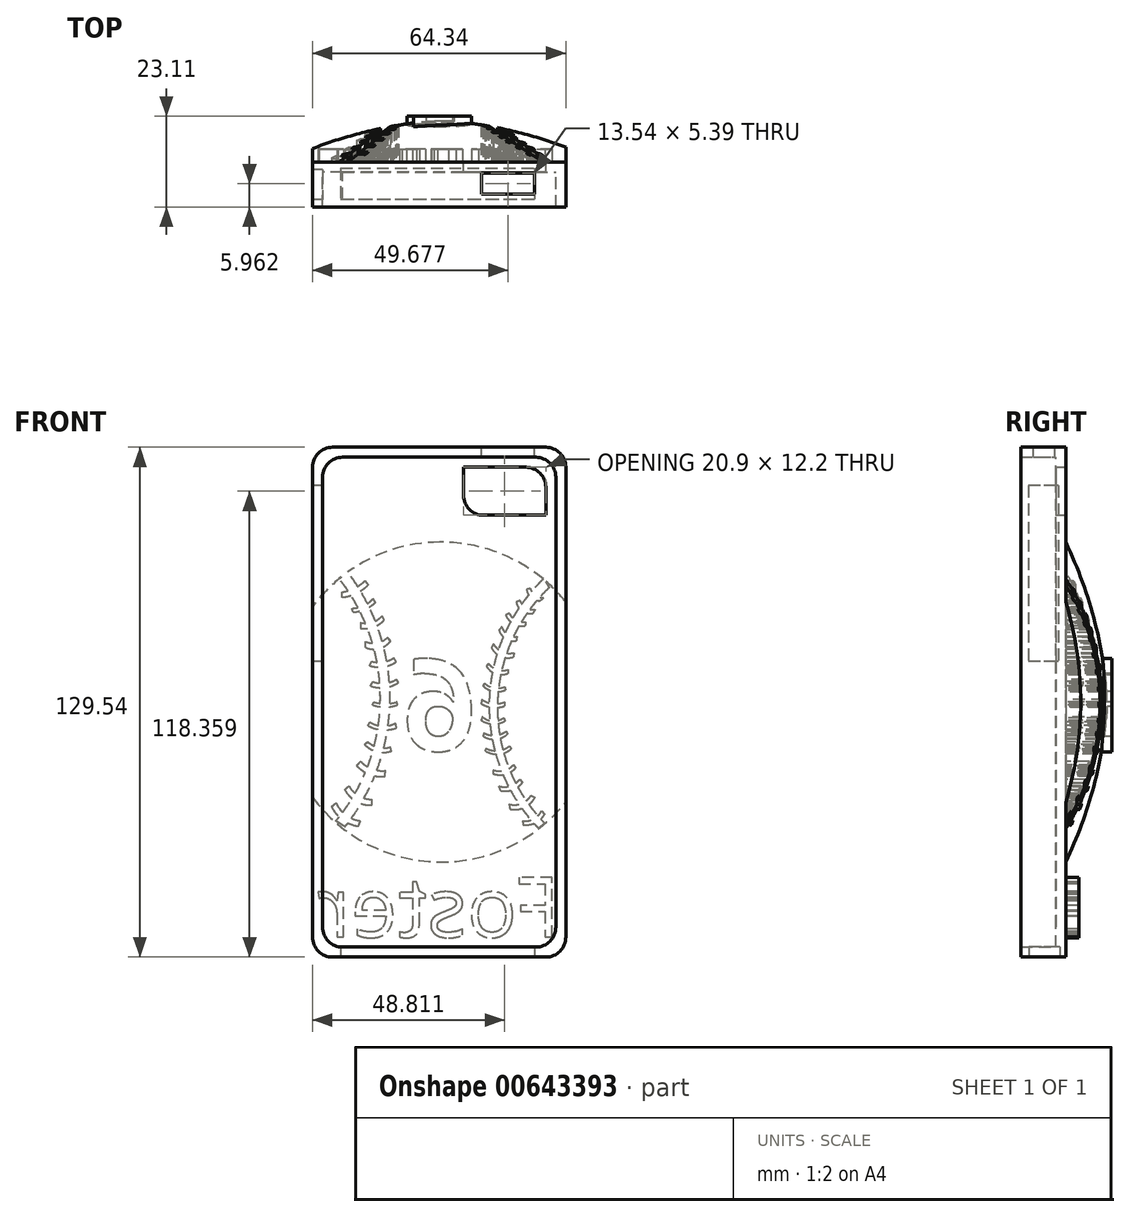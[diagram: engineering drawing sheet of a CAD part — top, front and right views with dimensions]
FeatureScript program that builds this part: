
annotation { "Feature Type Name" : "Feature", "Feature Type Description" : "" }
export const myFeature = defineFeature(function(context is Context, id is Id, definition is map)
    precondition{}
    {
        {
            var Q0;
            Q0=qCreatedBy(makeId("Front.planeOp"),FACE);
            var sketch = newSketch(context, id + "F0", { "sketchPlane" : qUnion([Q0])});
            skLineSegment(sketch, "E0", {"start": v(-32.65, 64.75) * mm, "end": v(-32.65, -64.8) * mm});
            skLineSegment(sketch, "E1", {"start": v(-32.65, -64.8) * mm, "end": v(31.7, -64.8) * mm});
            skLineSegment(sketch, "E2", {"start": v(31.7, -64.8) * mm, "end": v(31.7, 64.75) * mm});
            skLineSegment(sketch, "E3", {"start": v(31.7, 64.75) * mm, "end": v(-32.65, 64.75) * mm});
            skSolve(sketch);
        }
        {
            var Q0;
            Q0=qSketchRegion(id+"F0",true);
            extrude(context, id + "F1", {"entities" : qUnion([Q0]), "depth" : 11.43 * mm, "offsetDistance" : 25.4 * mm});
        }
        {
            var Q0;
            Q0=makeQuery(id+"F1.opExtrude","CAP_FACE",FACE,{"disambiguationData":[OSD([sQuery(id+"F0.wireOp",EDGE,"E0"),sQuery(id+"F0.wireOp",EDGE,"E1"),sQuery(id+"F0.wireOp",EDGE,"E2"),sQuery(id+"F0.wireOp",EDGE,"E3")])],"isStart":false});
            shell(context, id + "F2", {"entities" : qUnion([Q0]), "thickness" : 2.54 * mm});
        }
        {
            var Q0;
            Q0=makeQuery(id+"F2.opShell","OFFSET_EDGE",EDGE,{"disambiguationData":[OSD([sQuery(id+"F0.wireOp",EDGE,"E0"),sQuery(id+"F0.wireOp",EDGE,"E3")])]});
            var Q1;
            Q1=makeQuery(id+"F2.opShell","OFFSET_EDGE",EDGE,{"disambiguationData":[OSD([sQuery(id+"F0.wireOp",EDGE,"E2"),sQuery(id+"F0.wireOp",EDGE,"E3")])]});
            var Q2;
            Q2=makeQuery(id+"F1.opExtrude","SWEPT_EDGE",EDGE,{"disambiguationData":[OSD([sQuery(id+"F0.wireOp",EDGE,"E2"),sQuery(id+"F0.wireOp",EDGE,"E3")])]});
            var Q3;
            Q3=makeQuery(id+"F1.opExtrude","SWEPT_EDGE",EDGE,{"disambiguationData":[OSD([sQuery(id+"F0.wireOp",EDGE,"E0"),sQuery(id+"F0.wireOp",EDGE,"E3")])]});
            fillet(context, id + "F3", {"entities" : qUnion([Q0, Q1, Q2, Q3]), "radius" : 5.08 * mm, "tangentPropagation" : true, "allowEdgeOverflow" : false});
        }
        {
            var Q0;
            Q0=makeQuery(id+"F1.opExtrude","SWEPT_EDGE",EDGE,{"disambiguationData":[OSD([sQuery(id+"F0.wireOp",EDGE,"E0"),sQuery(id+"F0.wireOp",EDGE,"E1")])]});
            var Q1;
            Q1=makeQuery(id+"F1.opExtrude","SWEPT_EDGE",EDGE,{"disambiguationData":[OSD([sQuery(id+"F0.wireOp",EDGE,"E1"),sQuery(id+"F0.wireOp",EDGE,"E2")])]});
            var Q2;
            {var subQ0=sQuery(id+"F0.wireOp",EDGE,"E0");Q2=makeQuery(id+"FT8oDP2O1UVCOSW_1.boolean.opBoolean","SPLIT",EDGE,{"disambiguationData":[topologyDisambiguationEdgeConnected([makeQuery(id+"FT8oDP2O1UVCOSW_1.opExtrude","CAP_FACE",FACE,{"disambiguationData":[OSD([sQuery(id+"FKsIdxiG1m6IwAw_1.wireOp",EDGE,"Qu0jH38F-jogJ-LF4x-abM8-sLSAV8IaNlCL.bottom"),sQuery(id+"FKsIdxiG1m6IwAw_1.wireOp",EDGE,"Qu0jH38F-jogJ-LF4x-abM8-sLSAV8IaNlCL.top"),sQuery(id+"FKsIdxiG1m6IwAw_1.wireOp",EDGE,"Qu0jH38F-jogJ-LF4x-abM8-sLSAV8IaNlCL.left"),sQuery(id+"FKsIdxiG1m6IwAw_1.wireOp",EDGE,"Qu0jH38F-jogJ-LF4x-abM8-sLSAV8IaNlCL.right")])],"isStart":false})])],"derivedFrom":makeQuery(id+"F2.opShell","OFFSET_EDGE",EDGE,{"disambiguationData":[OSD([subQ0,sQuery(id+"F0.wireOp",EDGE,"E1")])]})});}
            var Q3;
            {var subQ0=sQuery(id+"F0.wireOp",EDGE,"E2");Q3=makeQuery(id+"FT8oDP2O1UVCOSW_1.boolean.opBoolean","SPLIT",EDGE,{"disambiguationData":[topologyDisambiguationEdgeConnected([makeQuery(id+"FT8oDP2O1UVCOSW_1.opExtrude","CAP_FACE",FACE,{"disambiguationData":[OSD([sQuery(id+"FKsIdxiG1m6IwAw_1.wireOp",EDGE,"Qu0jH38F-jogJ-LF4x-abM8-sLSAV8IaNlCL.bottom"),sQuery(id+"FKsIdxiG1m6IwAw_1.wireOp",EDGE,"Qu0jH38F-jogJ-LF4x-abM8-sLSAV8IaNlCL.top"),sQuery(id+"FKsIdxiG1m6IwAw_1.wireOp",EDGE,"Qu0jH38F-jogJ-LF4x-abM8-sLSAV8IaNlCL.left"),sQuery(id+"FKsIdxiG1m6IwAw_1.wireOp",EDGE,"Qu0jH38F-jogJ-LF4x-abM8-sLSAV8IaNlCL.right")])],"isStart":false})])],"derivedFrom":makeQuery(id+"F2.opShell","OFFSET_EDGE",EDGE,{"disambiguationData":[OSD([sQuery(id+"F0.wireOp",EDGE,"E1"),subQ0])]})});}
            fillet(context, id + "F4", {"entities" : qUnion([Q0, Q1, Q2, Q3]), "radius" : 5.08 * mm, "tangentPropagation" : true, "allowEdgeOverflow" : false});
        }
        {
            var Q0;
            Q0=makeQuery(id+"F1.opExtrude","SWEPT_FACE",FACE,{"disambiguationData":[OSD([sQuery(id+"F0.wireOp",EDGE,"E1")])]});
            var sketch = newSketch(context, id + "F5", { "sketchPlane" : qUnion([Q0])});
            skLineSegment(sketch, "E4.bottom", {"start": v(-25.48, 1.54) * mm, "end": v(23.7, 1.54) * mm});
            skLineSegment(sketch, "E4.top", {"start": v(-25.48, 9.42) * mm, "end": v(23.7, 9.42) * mm});
            skLineSegment(sketch, "E4.left", {"start": v(-25.48, 1.54) * mm, "end": v(-25.48, 9.42) * mm});
            skLineSegment(sketch, "E4.right", {"start": v(23.7, 1.54) * mm, "end": v(23.7, 9.42) * mm});
            skSolve(sketch);
        }
        {
            var Q0;
            Q0 = qSketchRegion(id + "F5", true);
            extrude(context, id + "F6", {"entities" : qUnion([Q0]), "operationType" : NewBodyOperationType.REMOVE, "oppositeDirection" : true, "depth" : 2.54 * mm, "offsetDistance" : 25.4 * mm});
        }
        {
            var Q0;
            Q0=makeQuery(id+"F1.opExtrude","SWEPT_FACE",FACE,{"disambiguationData":[OSD([sQuery(id+"F0.wireOp",EDGE,"E0")])]});
            var sketch = newSketch(context, id + "F7", { "sketchPlane" : qUnion([Q0])});
            skLineSegment(sketch, "E5.bottom", {"start": v(1.9, 55) * mm, "end": v(9.52, 55) * mm});
            skLineSegment(sketch, "E5.top", {"start": v(1.9, 10.3) * mm, "end": v(9.52, 10.3) * mm});
            skLineSegment(sketch, "E5.left", {"start": v(1.9, 55) * mm, "end": v(1.9, 10.3) * mm});
            skLineSegment(sketch, "E5.right", {"start": v(9.52, 55) * mm, "end": v(9.52, 10.3) * mm});
            skSolve(sketch);
        }
        {
            var Q0;
            Q0 = qSketchRegion(id + "F7", true);
            extrude(context, id + "F8", {"entities" : qUnion([Q0]), "operationType" : NewBodyOperationType.REMOVE, "oppositeDirection" : true, "depth" : 2.54 * mm, "offsetDistance" : 25.4 * mm});
        }
        {
            var Q0;
            Q0=makeQuery(id+"F1.opExtrude","SWEPT_FACE",FACE,{"disambiguationData":[OSD([sQuery(id+"F0.wireOp",EDGE,"E3")])]});
            var sketch = newSketch(context, id + "F9", { "sketchPlane" : qUnion([Q0])});
            skLineSegment(sketch, "E6.bottom", {"start": v(10.26, -8.16) * mm, "end": v(23.8, -8.16) * mm});
            skLineSegment(sketch, "E6.top", {"start": v(10.26, -2.77) * mm, "end": v(23.8, -2.77) * mm});
            skLineSegment(sketch, "E6.left", {"start": v(10.26, -8.16) * mm, "end": v(10.26, -2.77) * mm});
            skLineSegment(sketch, "E6.right", {"start": v(23.8, -8.16) * mm, "end": v(23.8, -2.77) * mm});
            skSolve(sketch);
        }
        {
            var Q0;
            Q0 = qSketchRegion(id + "F9", true);
            extrude(context, id + "F10", {"entities" : qUnion([Q0]), "operationType" : NewBodyOperationType.REMOVE, "oppositeDirection" : true, "depth" : 2.54 * mm, "offsetDistance" : 25.4 * mm});
        }
        {
            var Q0;
            Q0=makeQuery(id+"F1.opExtrude","CAP_FACE",FACE,{"disambiguationData":[OSD([sQuery(id+"F0.wireOp",EDGE,"E0"),sQuery(id+"F0.wireOp",EDGE,"E1"),sQuery(id+"F0.wireOp",EDGE,"E2"),sQuery(id+"F0.wireOp",EDGE,"E3")])],"isStart":true});
            var sketch = newSketch(context, id + "F11", { "sketchPlane" : qUnion([Q0])});
            skLineSegment(sketch, "E7.bottom", {"start": v(-26.61, 59.67) * mm, "end": v(-5.7, 59.67) * mm});
            skLineSegment(sketch, "E7.top", {"start": v(-26.61, 47.47) * mm, "end": v(-5.7, 47.47) * mm});
            skLineSegment(sketch, "E7.left", {"start": v(-26.61, 59.67) * mm, "end": v(-26.61, 47.47) * mm});
            skLineSegment(sketch, "E7.right", {"start": v(-5.7, 59.67) * mm, "end": v(-5.7, 47.47) * mm});
            skSolve(sketch);
        }
        {
            var Q0;
            Q0 = qSketchRegion(id + "F11", true);
            extrude(context, id + "F12", {"entities" : qUnion([Q0]), "operationType" : NewBodyOperationType.REMOVE, "oppositeDirection" : true, "depth" : 2.54 * mm, "offsetDistance" : 25.4 * mm});
        }
        {
            var Q0;
            Q0=makeQuery(id+"F12.boolean.opBoolean","COPY",EDGE,{"derivedFrom":makeQuery(id+"F12.opExtrude","SWEPT_EDGE",EDGE,{"disambiguationData":[OSD([sQuery(id+"F11.wireOp",EDGE,"E7.bottom"),sQuery(id+"F11.wireOp",EDGE,"E7.left")])]})});
            var Q1;
            Q1=makeQuery(id+"F12.boolean.opBoolean","COPY",EDGE,{"derivedFrom":makeQuery(id+"F12.opExtrude","SWEPT_EDGE",EDGE,{"disambiguationData":[OSD([sQuery(id+"F11.wireOp",EDGE,"E7.top"),sQuery(id+"F11.wireOp",EDGE,"E7.right")])]})});
            fillet(context, id + "F13", {"entities" : qUnion([Q0, Q1]), "radius" : 5.08 * mm, "tangentPropagation" : true, "allowEdgeOverflow" : false});
        }
        {
            var Q0;
            Q0=qCreatedBy(makeId("Right.planeOp"),FACE);
            var sketch = newSketch(context, id + "F14", { "sketchPlane" : qUnion([Q0])});
            skLineSegment(sketch, "E8", {"start": v(0, 0) * mm, "end": v(10.6, 0) * mm});
            skLineSegment(sketch, "E9", {"start": v(0, 0) * mm, "end": v(0, 40.64) * mm});
            skArc(sketch, "E10", {"start": v(10.6, 0) * mm, "mid": v(7.26, 20.83) * mm, "end": v(0, 40.64) * mm});
            skSolve(sketch);
        }
        {
            var Q0;
            Q0 = qSketchRegion(id + "F14", true);
            var Q1;
            Q1=sQuery(id+"F14.wireOp",EDGE,"E8");
            revolve(context, id + "F15", {"operationType" : NewBodyOperationType.ADD, "entities" : qUnion([Q0]), "axis" : qUnion([Q1]), "revolveType" : RevolveType.FULL});
        }
        {
            var Q0;
            {var subQ0=sQuery(id+"F0.wireOp",EDGE,"E2");Q0=makeQuery(id+"F15.boolean.opBoolean","SPLIT",FACE,{"disambiguationData":[TD([makeQuery(id+"F1.opExtrude","SWEPT_FACE",FACE,{"disambiguationData":[OSD([subQ0])]})])],"derivedFrom":makeQuery(id+"F15.opRevolve","SWEPT_FACE",FACE,{"disambiguationData":[OSD([sQuery(id+"F14.wireOp",EDGE,"E9")])]})});}
            var sketch = newSketch(context, id + "F16", { "sketchPlane" : qUnion([Q0])});
            skLineSegment(sketch, "E11", {"start": v(31.7, 25.44) * mm, "end": v(31.7, -25.44) * mm});
            skLineSegment(sketch, "E12", {"start": v(31.7, -25.44) * mm, "end": v(46.9, -25.44) * mm});
            skLineSegment(sketch, "E13", {"start": v(46.9, -25.44) * mm, "end": v(46.9, 25.44) * mm});
            skLineSegment(sketch, "E14", {"start": v(46.9, 25.44) * mm, "end": v(31.7, 25.44) * mm});
            skSolve(sketch);
        }
        {
            var Q0;
            Q0 = qSketchRegion(id + "F16", true);
            extrude(context, id + "F17", {"entities" : qUnion([Q0]), "operationType" : NewBodyOperationType.REMOVE, "oppositeDirection" : true, "depth" : 13.97 * mm, "offsetDistance" : 25.4 * mm});
        }
        {
            var Q0;
            {var subQ0=sQuery(id+"F0.wireOp",EDGE,"E0");Q0=makeQuery(id+"F15.boolean.opBoolean","SPLIT",FACE,{"disambiguationData":[TD([makeQuery(id+"F1.opExtrude","SWEPT_FACE",FACE,{"disambiguationData":[OSD([subQ0])]})])],"derivedFrom":makeQuery(id+"F15.opRevolve","SWEPT_FACE",FACE,{"disambiguationData":[OSD([sQuery(id+"F14.wireOp",EDGE,"E9")])]})});}
            var sketch = newSketch(context, id + "F18", { "sketchPlane" : qUnion([Q0])});
            skLineSegment(sketch, "E15", {"start": v(-32.65, 24.2) * mm, "end": v(-32.65, -24.2) * mm});
            skLineSegment(sketch, "E16", {"start": v(-32.65, -24.2) * mm, "end": v(-43.03, -24.2) * mm});
            skLineSegment(sketch, "E17", {"start": v(-43.03, -24.2) * mm, "end": v(-43.03, 24.2) * mm});
            skLineSegment(sketch, "E18", {"start": v(-43.03, 24.2) * mm, "end": v(-32.65, 24.2) * mm});
            skSolve(sketch);
        }
        {
            var Q0;
            Q0 = qSketchRegion(id + "F18", true);
            extrude(context, id + "F19", {"entities" : qUnion([Q0]), "operationType" : NewBodyOperationType.REMOVE, "oppositeDirection" : true, "depth" : 11.43 * mm, "offsetDistance" : 25.4 * mm});
        }
        {
            var Q0;
            Q0=qCreatedBy(makeId("Front.planeOp"),FACE);
            var sketch = newSketch(context, id + "F20", { "sketchPlane" : qUnion([Q0])});
            skArc(sketch, "E19", {"start": v(-24.38, -31.68) * mm, "mid": v(-12.98, 0.63) * mm, "end": v(-23.8, 33.14) * mm});
            skArc(sketch, "E20", {"start": v(-26.72, -30.22) * mm, "mid": v(-15.42, 0.4) * mm, "end": v(-25.86, 31.31) * mm});
            skLineSegment(sketch, "E21", {"start": v(-23.8, 33.14) * mm, "end": v(-25.86, 31.31) * mm});
            skLineSegment(sketch, "E22", {"start": v(-24.38, -31.68) * mm, "end": v(-26.72, -30.22) * mm});
            skLineSegment(sketch, "E23", {"start": v(-25.86, 31.31) * mm, "end": v(-23.8, 33.14) * mm});
            skSolve(sketch);
        }
        {
            var Q0;
            Q0=qCreatedBy(makeId("Front.planeOp"),FACE);
            var sketch = newSketch(context, id + "F21", { "sketchPlane" : qUnion([Q0])});
            skLineSegment(sketch, "E24", {"start": v(32.56, -30.8) * mm, "end": v(26.43, -30.8) * mm});
            skArc(sketch, "E25", {"start": v(27.55, 29.14) * mm, "mid": v(14.35, -0.61) * mm, "end": v(26.4, -30.85) * mm});
            skArc(sketch, "E26", {"start": v(26.22, 31.47) * mm, "mid": v(12.23, 0) * mm, "end": v(24.78, -32.1) * mm});
            skLineSegment(sketch, "E27", {"start": v(26.43, -30.8) * mm, "end": v(24.78, -32.1) * mm});
            skLineSegment(sketch, "E28", {"start": v(27.55, 29.14) * mm, "end": v(26.22, 31.47) * mm});
            skSolve(sketch);
        }
        {
            var Q0;
            Q0=makeQuery(id+"F20.imprint","IMPRINT",FACE,{"disambiguationData":[TD([[makeQuery(id+"F20.imprint","IMPRINT",EDGE,{"derivedFrom":sQuery(id+"F20.wireOp",EDGE,"E19")}),1.0]])]});
            extrude(context, id + "F22", {"entities" : qUnion([Q0]), "operationType" : NewBodyOperationType.REMOVE, "oppositeDirection" : true, "depth" : 25.4 * mm, "offsetDistance" : 25.4 * mm});
        }
        {
            var Q0;
            {var subQ4=sQuery(id+"F21.wireOp",EDGE,"E26");Q0=makeQuery(id+"F21.imprint","IMPRINT",FACE,{"disambiguationData":[TD([[makeQuery(id+"F21.imprint","IMPRINT",EDGE,{"derivedFrom":subQ4}),1.0]])]});}
            extrude(context, id + "F23", {"entities" : qUnion([Q0]), "operationType" : NewBodyOperationType.REMOVE, "oppositeDirection" : true, "depth" : 13.72 * mm, "offsetDistance" : 25.4 * mm});
        }
        {
            var Q0;
            Q0=qCreatedBy(makeId("Front.planeOp"),FACE);
            var sketch = newSketch(context, id + "F24", { "sketchPlane" : qUnion([Q0])});
            skArc(sketch, "E29", {"start": v(13.33, 14.78) * mm, "mid": v(15.54, 12.78) * mm, "end": v(18.5, 12.52) * mm});
            skArc(sketch, "E30", {"start": v(12.8, 13.85) * mm, "mid": v(15.18, 11.6) * mm, "end": v(18.44, 11.46) * mm});
            skPoint(sketch, "E30.midSnap0", {"position": v(15.54, 12.78) * mm});
            skArc(sketch, "E31", {"start": v(12.05, 9.81) * mm, "mid": v(14.3, 8.24) * mm, "end": v(17.03, 8.25) * mm});
            skArc(sketch, "E32", {"start": v(11.51, 9.17) * mm, "mid": v(13.91, 7.17) * mm, "end": v(17.03, 7.33) * mm});
            skArc(sketch, "E33", {"start": v(11.1, 4.73) * mm, "mid": v(13.54, 3.58) * mm, "end": v(16.22, 3.9) * mm});
            skArc(sketch, "E34", {"start": v(10.61, 4.18) * mm, "mid": v(13.31, 2.72) * mm, "end": v(16.36, 3.07) * mm});
            skArc(sketch, "E35", {"start": v(10.38, 0.62) * mm, "mid": v(13.18, -0.4) * mm, "end": v(16.14, 0) * mm});
            skArc(sketch, "E36", {"start": v(10.16, -0.4) * mm, "mid": v(13.06, -1.38) * mm, "end": v(16.1, -1.01) * mm});
            skLineSegment(sketch, "E37", {"start": v(17.03, 8.25) * mm, "end": v(17.03, 7.33) * mm});
            skLineSegment(sketch, "E38", {"start": v(12.05, 9.81) * mm, "end": v(11.51, 9.17) * mm});
            skLineSegment(sketch, "E39", {"start": v(16.22, 3.9) * mm, "end": v(16.36, 3.07) * mm});
            skLineSegment(sketch, "E40", {"start": v(11.1, 4.73) * mm, "end": v(10.61, 4.18) * mm});
            skLineSegment(sketch, "E41", {"start": v(10.38, 0.62) * mm, "end": v(10.16, -0.4) * mm});
            skLineSegment(sketch, "E42", {"start": v(16.14, 0) * mm, "end": v(16.1, -1.01) * mm});
            skLineSegment(sketch, "E43", {"start": v(18.5, 12.52) * mm, "end": v(18.44, 11.46) * mm});
            skLineSegment(sketch, "E44", {"start": v(13.33, 14.78) * mm, "end": v(12.8, 13.85) * mm});
            skArc(sketch, "E45", {"start": v(10.48, -3.76) * mm, "mid": v(13.2, -4.8) * mm, "end": v(15.97, -4) * mm});
            skArc(sketch, "E46", {"start": v(10.2, -4.62) * mm, "mid": v(13.17, -5.57) * mm, "end": v(16.2, -4.85) * mm});
            skArc(sketch, "E47", {"start": v(10.92, -7.86) * mm, "mid": v(13.8, -8.47) * mm, "end": v(16.55, -7.4) * mm});
            skArc(sketch, "E48", {"start": v(10.69, -8.65) * mm, "mid": v(13.88, -9.46) * mm, "end": v(16.89, -8.14) * mm});
            skArc(sketch, "E49", {"start": v(11.41, -11.78) * mm, "mid": v(14.5, -12.35) * mm, "end": v(17.41, -11.16) * mm});
            skArc(sketch, "E50", {"start": v(11.17, -12.35) * mm, "mid": v(14.58, -13.24) * mm, "end": v(17.84, -11.9) * mm});
            skPoint(sketch, "E50.startSnap0", {"position": v(14.5, -12.35) * mm});
            skArc(sketch, "E51", {"start": v(17.27, -25.92) * mm, "mid": v(20.45, -25.78) * mm, "end": v(22.88, -23.72) * mm});
            skArc(sketch, "E52", {"start": v(17.5, -27.2) * mm, "mid": v(21.17, -26.78) * mm, "end": v(23.85, -24.27) * mm});
            skArc(sketch, "E53", {"start": v(20.73, -30.15) * mm, "mid": v(23.54, -29.72) * mm, "end": v(25.5, -27.67) * mm});
            skArc(sketch, "E54", {"start": v(20.82, -31.16) * mm, "mid": v(24, -30.69) * mm, "end": v(26.33, -28.5) * mm});
            skLineSegment(sketch, "E55", {"start": v(22.88, -23.72) * mm, "end": v(23.85, -24.27) * mm});
            skLineSegment(sketch, "E56", {"start": v(17.27, -25.92) * mm, "end": v(17.5, -27.2) * mm});
            skLineSegment(sketch, "E57", {"start": v(15.97, -4) * mm, "end": v(16.2, -4.85) * mm});
            skLineSegment(sketch, "E58", {"start": v(10.48, -3.76) * mm, "end": v(10.2, -4.62) * mm});
            skLineSegment(sketch, "E59", {"start": v(16.55, -7.4) * mm, "end": v(16.89, -8.14) * mm});
            skLineSegment(sketch, "E60", {"start": v(10.92, -7.86) * mm, "end": v(10.69, -8.65) * mm});
            skLineSegment(sketch, "E61", {"start": v(11.41, -11.78) * mm, "end": v(11.17, -12.35) * mm});
            skLineSegment(sketch, "E62", {"start": v(17.41, -11.16) * mm, "end": v(17.84, -11.9) * mm});
            skLineSegment(sketch, "E63", {"start": v(20.73, -30.15) * mm, "end": v(20.82, -31.16) * mm});
            skLineSegment(sketch, "E64", {"start": v(25.5, -27.67) * mm, "end": v(26.33, -28.5) * mm});
            skArc(sketch, "E65", {"start": v(13.3, -17.27) * mm, "mid": v(16.06, -17.4) * mm, "end": v(18.4, -15.92) * mm});
            skArc(sketch, "E66", {"start": v(13.15, -18.19) * mm, "mid": v(16.27, -18.34) * mm, "end": v(18.96, -16.77) * mm});
            skArc(sketch, "E67", {"start": v(14.78, -21.37) * mm, "mid": v(17.67, -21.3) * mm, "end": v(20.02, -19.6) * mm});
            skArc(sketch, "E68", {"start": v(15.14, -22.5) * mm, "mid": v(18.18, -22.3) * mm, "end": v(20.66, -20.52) * mm});
            skLineSegment(sketch, "E69", {"start": v(13.3, -17.27) * mm, "end": v(13.15, -18.19) * mm});
            skLineSegment(sketch, "E70", {"start": v(18.4, -15.92) * mm, "end": v(18.96, -16.77) * mm});
            skLineSegment(sketch, "E71", {"start": v(20.02, -19.6) * mm, "end": v(20.66, -20.52) * mm});
            skLineSegment(sketch, "E72", {"start": v(15.14, -22.5) * mm, "end": v(14.78, -21.37) * mm});
            skArc(sketch, "E73", {"start": v(14.7, 18.26) * mm, "mid": v(16.42, 16.12) * mm, "end": v(19.1, 15.52) * mm});
            skArc(sketch, "E74", {"start": v(15.44, 19.09) * mm, "mid": v(16.92, 17.17) * mm, "end": v(19.28, 16.62) * mm});
            skArc(sketch, "E75", {"start": v(16.42, 22.1) * mm, "mid": v(18.44, 19.9) * mm, "end": v(21.39, 19.36) * mm});
            skPoint(sketch, "E75.startSnap0", {"position": v(16.42, 16.12) * mm});
            skArc(sketch, "E76", {"start": v(17.36, 22.56) * mm, "mid": v(19.03, 20.73) * mm, "end": v(21.48, 20.37) * mm});
            skArc(sketch, "E77", {"start": v(19.1, 25.4) * mm, "mid": v(20.63, 23.14) * mm, "end": v(23.3, 22.56) * mm});
            skArc(sketch, "E78", {"start": v(20.02, 25.77) * mm, "mid": v(21.57, 24) * mm, "end": v(23.86, 23.48) * mm});
            skArc(sketch, "E79", {"start": v(21.75, 28.6) * mm, "mid": v(22.94, 26.44) * mm, "end": v(25.32, 25.77) * mm});
            skArc(sketch, "E80", {"start": v(22.67, 28.88) * mm, "mid": v(23.94, 27.1) * mm, "end": v(26.05, 26.59) * mm});
            skLineSegment(sketch, "E81", {"start": v(19.28, 16.62) * mm, "end": v(19.1, 15.52) * mm});
            skLineSegment(sketch, "E82", {"start": v(15.44, 19.09) * mm, "end": v(14.7, 18.26) * mm});
            skLineSegment(sketch, "E83", {"start": v(17.36, 22.56) * mm, "end": v(16.42, 22.1) * mm});
            skLineSegment(sketch, "E84", {"start": v(21.48, 20.37) * mm, "end": v(21.39, 19.36) * mm});
            skLineSegment(sketch, "E85", {"start": v(23.86, 23.48) * mm, "end": v(23.3, 22.56) * mm});
            skLineSegment(sketch, "E86", {"start": v(20.02, 25.77) * mm, "end": v(19.1, 25.4) * mm});
            skLineSegment(sketch, "E87", {"start": v(26.05, 26.59) * mm, "end": v(25.32, 25.77) * mm});
            skLineSegment(sketch, "E88", {"start": v(22.67, 28.88) * mm, "end": v(21.75, 28.6) * mm});
            skLineSegment(sketch, "E89.MirrorCS", {"start": v(-12.05, 9.81) * mm, "end": v(-11.51, 9.17) * mm});
            skSolve(sketch);
        }
        {
            var Q0;
            Q0 = qSketchRegion(id + "F24", true);
            extrude(context, id + "F25", {"entities" : qUnion([Q0]), "operationType" : NewBodyOperationType.REMOVE, "oppositeDirection" : true, "depth" : 25.4 * mm, "offsetDistance" : 25.4 * mm});
        }
        {
            var Q0;
            Q0=qCreatedBy(makeId("Front.planeOp"),FACE);
            var sketch = newSketch(context, id + "F26", { "sketchPlane" : qUnion([Q0])});
            skArc(sketch, "E90", {"start": v(-25.18, 27.94) * mm, "mid": v(-22, 28.92) * mm, "end": v(-19.29, 30.82) * mm});
            skArc(sketch, "E91", {"start": v(-25.18, 26.63) * mm, "mid": v(-21.56, 27.6) * mm, "end": v(-18.5, 29.77) * mm});
            skLineSegment(sketch, "E92", {"start": v(-25.18, 26.63) * mm, "end": v(-25.18, 27.94) * mm});
            skLineSegment(sketch, "E93", {"start": v(-19.29, 30.82) * mm, "end": v(-18.5, 29.77) * mm});
            skArc(sketch, "E94", {"start": v(-22.64, 23.82) * mm, "mid": v(-19.67, 24.49) * mm, "end": v(-17.23, 26.29) * mm});
            skArc(sketch, "E95", {"start": v(-22.34, 22.83) * mm, "mid": v(-19.3, 23.61) * mm, "end": v(-16.64, 25.3) * mm});
            skLineSegment(sketch, "E96", {"start": v(-16.64, 25.3) * mm, "end": v(-17.23, 26.29) * mm});
            skLineSegment(sketch, "E97", {"start": v(-22.34, 22.83) * mm, "end": v(-22.64, 23.82) * mm});
            skArc(sketch, "E98", {"start": v(-20.41, 20.2) * mm, "mid": v(-17.45, 20.26) * mm, "end": v(-14.98, 21.9) * mm});
            skArc(sketch, "E99", {"start": v(-20.41, 18.73) * mm, "mid": v(-17.14, 19.04) * mm, "end": v(-14.41, 20.88) * mm});
            skLineSegment(sketch, "E100", {"start": v(-14.41, 20.88) * mm, "end": v(-14.98, 21.9) * mm});
            skLineSegment(sketch, "E101", {"start": v(-20.41, 20.2) * mm, "end": v(-20.41, 18.73) * mm});
            skPoint(sketch, "E102.endSnap0", {"position": v(-15.84, 15.35) * mm});
            skPoint(sketch, "E103.endSnap0", {"position": v(-14.7, 8.8) * mm});
            skArc(sketch, "E104", {"start": v(-17.26, 5.19) * mm, "mid": v(-14.22, 4.77) * mm, "end": v(-11.32, 5.78) * mm});
            skArc(sketch, "E105", {"start": v(-17.94, 4.12) * mm, "mid": v(-14.28, 3.68) * mm, "end": v(-10.82, 4.95) * mm});
            skLineSegment(sketch, "E106", {"start": v(-10.82, 4.95) * mm, "end": v(-11.32, 5.78) * mm});
            skLineSegment(sketch, "E107", {"start": v(-17.94, 4.12) * mm, "end": v(-17.26, 5.19) * mm});
            skArc(sketch, "E108", {"start": v(-20.43, -15.07) * mm, "mid": v(-17.54, -16.99) * mm, "end": v(-14.11, -17.42) * mm});
            skArc(sketch, "E109", {"start": v(-21.4, -16.16) * mm, "mid": v(-18.14, -18.4) * mm, "end": v(-14.22, -18.88) * mm});
            skLineSegment(sketch, "E110", {"start": v(-14.22, -18.88) * mm, "end": v(-14.11, -17.42) * mm});
            skLineSegment(sketch, "E111", {"start": v(-21.4, -16.16) * mm, "end": v(-20.43, -15.07) * mm});
            skPoint(sketch, "E112.endSnap0", {"position": v(-15.94, -12.85) * mm});
            skArc(sketch, "E113", {"start": v(-26.63, -25.65) * mm, "mid": v(-24.15, -28.73) * mm, "end": v(-20.47, -30.16) * mm});
            skArc(sketch, "E114", {"start": v(-27.83, -26.5) * mm, "mid": v(-25.06, -29.89) * mm, "end": v(-21, -31.53) * mm});
            skLineSegment(sketch, "E115", {"start": v(-21, -31.53) * mm, "end": v(-20.47, -30.16) * mm});
            skLineSegment(sketch, "E116", {"start": v(-27.83, -26.5) * mm, "end": v(-26.63, -25.65) * mm});
            skArc(sketch, "E117", {"start": v(-23.38, -21.29) * mm, "mid": v(-20.93, -23.82) * mm, "end": v(-17.52, -24.71) * mm});
            skArc(sketch, "E118", {"start": v(-24.42, -22.32) * mm, "mid": v(-21.53, -25.26) * mm, "end": v(-17.52, -26.18) * mm});
            skLineSegment(sketch, "E119", {"start": v(-17.52, -26.18) * mm, "end": v(-17.52, -24.71) * mm});
            skLineSegment(sketch, "E120", {"start": v(-24.42, -22.32) * mm, "end": v(-23.38, -21.29) * mm});
            skArc(sketch, "E121", {"start": v(-19.14, 15.35) * mm, "mid": v(-16.22, 15.04) * mm, "end": v(-13.61, 16.39) * mm});
            skArc(sketch, "E122", {"start": v(-19.14, 13.88) * mm, "mid": v(-15.66, 13.58) * mm, "end": v(-12.79, 15.56) * mm});
            skLineSegment(sketch, "E123", {"start": v(-12.79, 15.56) * mm, "end": v(-13.61, 16.39) * mm});
            skLineSegment(sketch, "E124", {"start": v(-19.14, 13.88) * mm, "end": v(-19.14, 15.35) * mm});
            skArc(sketch, "E125", {"start": v(-17.04, 0) * mm, "mid": v(-14.14, -0.42) * mm, "end": v(-11.24, 0) * mm});
            skArc(sketch, "E126", {"start": v(-17.36, -0.72) * mm, "mid": v(-14.19, -1.27) * mm, "end": v(-11, -0.72) * mm});
            skLineSegment(sketch, "E127", {"start": v(-11, -0.72) * mm, "end": v(-11.24, 0) * mm});
            skLineSegment(sketch, "E128", {"start": v(-17.36, -0.72) * mm, "end": v(-17.04, 0) * mm});
            skArc(sketch, "E129", {"start": v(-17.62, 10.3) * mm, "mid": v(-14.7, 10.18) * mm, "end": v(-11.95, 11.22) * mm});
            skArc(sketch, "E130", {"start": v(-18.1, 9.25) * mm, "mid": v(-14.62, 8.95) * mm, "end": v(-11.37, 10.21) * mm});
            skLineSegment(sketch, "E131", {"start": v(-11.37, 10.21) * mm, "end": v(-11.95, 11.22) * mm});
            skLineSegment(sketch, "E132", {"start": v(-18.1, 9.25) * mm, "end": v(-17.62, 10.3) * mm});
            skArc(sketch, "E133", {"start": v(-18, -5.11) * mm, "mid": v(-14.8, -6.1) * mm, "end": v(-11.55, -5.35) * mm});
            skArc(sketch, "E134", {"start": v(-18.59, -5.99) * mm, "mid": v(-15, -7.06) * mm, "end": v(-11.3, -6.55) * mm});
            skLineSegment(sketch, "E135", {"start": v(-11.3, -6.55) * mm, "end": v(-11.55, -5.35) * mm});
            skLineSegment(sketch, "E136", {"start": v(-18.59, -5.99) * mm, "end": v(-18, -5.11) * mm});
            skArc(sketch, "E137", {"start": v(-18.65, -10.08) * mm, "mid": v(-15.92, -11.5) * mm, "end": v(-12.84, -11.44) * mm});
            skArc(sketch, "E138", {"start": v(-19.45, -10.77) * mm, "mid": v(-16.27, -12.6) * mm, "end": v(-12.61, -12.47) * mm});
            skLineSegment(sketch, "E139", {"start": v(-12.61, -12.47) * mm, "end": v(-12.84, -11.44) * mm});
            skLineSegment(sketch, "E140", {"start": v(-19.45, -10.77) * mm, "end": v(-18.65, -10.08) * mm});
            skSolve(sketch);
        }
        {
            var Q0;
            Q0 = qSketchRegion(id + "F26", true);
            extrude(context, id + "F27", {"entities" : qUnion([Q0]), "operationType" : NewBodyOperationType.REMOVE, "oppositeDirection" : true, "depth" : 11.18 * mm, "offsetDistance" : 25.4 * mm});
        }
        {
            var Q0;
            {var subQ0=sQuery(id+"F0.wireOp",EDGE,"E2");var subQ1=sQuery(id+"F0.wireOp",EDGE,"E1");var subQ2=sQuery(id+"F0.wireOp",EDGE,"E0");Q0=makeQuery(id+"F15.boolean.opBoolean","SPLIT",FACE,{"disambiguationData":[TD([makeQuery(id+"F1.opExtrude","SWEPT_FACE",FACE,{"disambiguationData":[OSD([subQ1])]})])],"derivedFrom":makeQuery(id+"F1.opExtrude","CAP_FACE",FACE,{"disambiguationData":[OSD([subQ2,subQ1,subQ0,sQuery(id+"F0.wireOp",EDGE,"E3")])],"isStart":true})});}
            var sketch = newSketch(context, id + "F28", { "sketchPlane" : qUnion([Q0])});
            skText(sketch, "E141", { "text": "Foster", "fontName": "OpenSans-Regular.ttf"});
            const initialGuessF28  = {"E141": [-0.03029, -0.05971, 1, 0, 0.01526]};
            skSetInitialGuess(sketch, initialGuessF28);
            skSolve(sketch);
        }
        {
            var Q0;
            Q0 = qSketchRegion(id + "F28", true);
            extrude(context, id + "F29", {"entities" : qUnion([Q0]), "operationType" : NewBodyOperationType.ADD, "depth" : 3.3 * mm, "offsetDistance" : 25.4 * mm});
        }
        {
            var Q0;
            {var subQ2=sQuery(id+"F0.wireOp",EDGE,"E3");var subQ3=sQuery(id+"F0.wireOp",EDGE,"E2");var subQ6=sQuery(id+"F0.wireOp",EDGE,"E0");Q0=makeQuery(id+"F27.boolean.opBoolean","MERGE",FACE,{"derivedFrom":[makeQuery(id+"F25.boolean.opBoolean","MERGE",FACE,{"derivedFrom":[makeQuery(id+"F23.boolean.opBoolean","MERGE",FACE,{"derivedFrom":[makeQuery(id+"F22.boolean.opBoolean","MERGE",FACE,{"derivedFrom":[makeQuery(id+"F15.boolean.opBoolean","SPLIT",FACE,{"disambiguationData":[TD([makeQuery(id+"F1.opExtrude","SWEPT_FACE",FACE,{"disambiguationData":[OSD([subQ2])]})])],"derivedFrom":makeQuery(id+"F1.opExtrude","CAP_FACE",FACE,{"disambiguationData":[OSD([subQ6,sQuery(id+"F0.wireOp",EDGE,"E1"),subQ3,subQ2])],"isStart":true})}),makeQuery(id+"F22.opExtrude","CAP_FACE",FACE,{"disambiguationData":[OSD([sQuery(id+"F20.wireOp",EDGE,"E19"),sQuery(id+"F20.wireOp",EDGE,"E20"),sQuery(id+"F20.wireOp",EDGE,"E22"),sQuery(id+"F20.wireOp",EDGE,"E23")])],"isStart":true})]}),makeQuery(id+"F23.opExtrude","CAP_FACE",FACE,{"disambiguationData":[OSD([sQuery(id+"F21.wireOp",EDGE,"E25"),sQuery(id+"F21.wireOp",EDGE,"E26"),sQuery(id+"F21.wireOp",EDGE,"E27"),sQuery(id+"F21.wireOp",EDGE,"E28")])],"isStart":true})]}),makeQuery(id+"F25.opExtrude","CAP_FACE",FACE,{"disambiguationData":[OSD([sQuery(id+"F24.wireOp",EDGE,"E29"),sQuery(id+"F24.wireOp",EDGE,"E30"),sQuery(id+"F24.wireOp",EDGE,"E43"),sQuery(id+"F24.wireOp",EDGE,"E44")])],"isStart":true}),makeQuery(id+"F25.opExtrude","CAP_FACE",FACE,{"disambiguationData":[OSD([sQuery(id+"F24.wireOp",EDGE,"E31"),sQuery(id+"F24.wireOp",EDGE,"E32"),sQuery(id+"F24.wireOp",EDGE,"E37"),sQuery(id+"F24.wireOp",EDGE,"E38")])],"isStart":true}),makeQuery(id+"F25.opExtrude","CAP_FACE",FACE,{"disambiguationData":[OSD([sQuery(id+"F24.wireOp",EDGE,"E33"),sQuery(id+"F24.wireOp",EDGE,"E34"),sQuery(id+"F24.wireOp",EDGE,"E39"),sQuery(id+"F24.wireOp",EDGE,"E40")])],"isStart":true}),makeQuery(id+"F25.opExtrude","CAP_FACE",FACE,{"disambiguationData":[OSD([sQuery(id+"F24.wireOp",EDGE,"E35"),sQuery(id+"F24.wireOp",EDGE,"E36"),sQuery(id+"F24.wireOp",EDGE,"E41"),sQuery(id+"F24.wireOp",EDGE,"E42")])],"isStart":true}),makeQuery(id+"F25.opExtrude","CAP_FACE",FACE,{"disambiguationData":[OSD([sQuery(id+"F24.wireOp",EDGE,"E45"),sQuery(id+"F24.wireOp",EDGE,"E46"),sQuery(id+"F24.wireOp",EDGE,"E57"),sQuery(id+"F24.wireOp",EDGE,"E58")])],"isStart":true}),makeQuery(id+"F25.opExtrude","CAP_FACE",FACE,{"disambiguationData":[OSD([sQuery(id+"F24.wireOp",EDGE,"E47"),sQuery(id+"F24.wireOp",EDGE,"E48"),sQuery(id+"F24.wireOp",EDGE,"E59"),sQuery(id+"F24.wireOp",EDGE,"E60")])],"isStart":true}),makeQuery(id+"F25.opExtrude","CAP_FACE",FACE,{"disambiguationData":[OSD([sQuery(id+"F24.wireOp",EDGE,"E49"),sQuery(id+"F24.wireOp",EDGE,"E50"),sQuery(id+"F24.wireOp",EDGE,"E61"),sQuery(id+"F24.wireOp",EDGE,"E62")])],"isStart":true}),makeQuery(id+"F25.opExtrude","CAP_FACE",FACE,{"disambiguationData":[OSD([sQuery(id+"F24.wireOp",EDGE,"E51"),sQuery(id+"F24.wireOp",EDGE,"E52"),sQuery(id+"F24.wireOp",EDGE,"E55"),sQuery(id+"F24.wireOp",EDGE,"E56")])],"isStart":true}),makeQuery(id+"F25.opExtrude","CAP_FACE",FACE,{"disambiguationData":[OSD([sQuery(id+"F24.wireOp",EDGE,"E53"),sQuery(id+"F24.wireOp",EDGE,"E54"),sQuery(id+"F24.wireOp",EDGE,"E63"),sQuery(id+"F24.wireOp",EDGE,"E64")])],"isStart":true}),makeQuery(id+"F25.opExtrude","CAP_FACE",FACE,{"disambiguationData":[OSD([sQuery(id+"F24.wireOp",EDGE,"E65"),sQuery(id+"F24.wireOp",EDGE,"E66"),sQuery(id+"F24.wireOp",EDGE,"E69"),sQuery(id+"F24.wireOp",EDGE,"E70")])],"isStart":true}),makeQuery(id+"F25.opExtrude","CAP_FACE",FACE,{"disambiguationData":[OSD([sQuery(id+"F24.wireOp",EDGE,"E67"),sQuery(id+"F24.wireOp",EDGE,"E68"),sQuery(id+"F24.wireOp",EDGE,"E71"),sQuery(id+"F24.wireOp",EDGE,"E72")])],"isStart":true}),makeQuery(id+"F25.opExtrude","CAP_FACE",FACE,{"disambiguationData":[OSD([sQuery(id+"F24.wireOp",EDGE,"E73"),sQuery(id+"F24.wireOp",EDGE,"E74"),sQuery(id+"F24.wireOp",EDGE,"E81"),sQuery(id+"F24.wireOp",EDGE,"E82")])],"isStart":true}),makeQuery(id+"F25.opExtrude","CAP_FACE",FACE,{"disambiguationData":[OSD([sQuery(id+"F24.wireOp",EDGE,"E75"),sQuery(id+"F24.wireOp",EDGE,"E76"),sQuery(id+"F24.wireOp",EDGE,"E83"),sQuery(id+"F24.wireOp",EDGE,"E84")])],"isStart":true}),makeQuery(id+"F25.opExtrude","CAP_FACE",FACE,{"disambiguationData":[OSD([sQuery(id+"F24.wireOp",EDGE,"E77"),sQuery(id+"F24.wireOp",EDGE,"E78"),sQuery(id+"F24.wireOp",EDGE,"E85"),sQuery(id+"F24.wireOp",EDGE,"E86")])],"isStart":true}),makeQuery(id+"F25.opExtrude","CAP_FACE",FACE,{"disambiguationData":[OSD([sQuery(id+"F24.wireOp",EDGE,"E79"),sQuery(id+"F24.wireOp",EDGE,"E80"),sQuery(id+"F24.wireOp",EDGE,"E87"),sQuery(id+"F24.wireOp",EDGE,"E88")])],"isStart":true})]}),makeQuery(id+"F27.opExtrude","CAP_FACE",FACE,{"disambiguationData":[OSD([sQuery(id+"F26.wireOp",EDGE,"E90"),sQuery(id+"F26.wireOp",EDGE,"E91"),sQuery(id+"F26.wireOp",EDGE,"E92"),sQuery(id+"F26.wireOp",EDGE,"E93")])],"isStart":true}),makeQuery(id+"F27.opExtrude","CAP_FACE",FACE,{"disambiguationData":[OSD([sQuery(id+"F26.wireOp",EDGE,"E94"),sQuery(id+"F26.wireOp",EDGE,"E95"),sQuery(id+"F26.wireOp",EDGE,"E96"),sQuery(id+"F26.wireOp",EDGE,"E97")])],"isStart":true}),makeQuery(id+"F27.opExtrude","CAP_FACE",FACE,{"disambiguationData":[OSD([sQuery(id+"F26.wireOp",EDGE,"E98"),sQuery(id+"F26.wireOp",EDGE,"E99"),sQuery(id+"F26.wireOp",EDGE,"E100"),sQuery(id+"F26.wireOp",EDGE,"E101")])],"isStart":true}),makeQuery(id+"F27.opExtrude","CAP_FACE",FACE,{"disambiguationData":[OSD([sQuery(id+"F26.wireOp",EDGE,"E104"),sQuery(id+"F26.wireOp",EDGE,"E105"),sQuery(id+"F26.wireOp",EDGE,"E106"),sQuery(id+"F26.wireOp",EDGE,"E107")])],"isStart":true}),makeQuery(id+"F27.opExtrude","CAP_FACE",FACE,{"disambiguationData":[OSD([sQuery(id+"F26.wireOp",EDGE,"E108"),sQuery(id+"F26.wireOp",EDGE,"E109"),sQuery(id+"F26.wireOp",EDGE,"E110"),sQuery(id+"F26.wireOp",EDGE,"E111")])],"isStart":true}),makeQuery(id+"F27.opExtrude","CAP_FACE",FACE,{"disambiguationData":[OSD([sQuery(id+"F26.wireOp",EDGE,"E113"),sQuery(id+"F26.wireOp",EDGE,"E114"),sQuery(id+"F26.wireOp",EDGE,"E115"),sQuery(id+"F26.wireOp",EDGE,"E116")])],"isStart":true}),makeQuery(id+"F27.opExtrude","CAP_FACE",FACE,{"disambiguationData":[OSD([sQuery(id+"F26.wireOp",EDGE,"E117"),sQuery(id+"F26.wireOp",EDGE,"E118"),sQuery(id+"F26.wireOp",EDGE,"E119"),sQuery(id+"F26.wireOp",EDGE,"E120")])],"isStart":true}),makeQuery(id+"F27.opExtrude","CAP_FACE",FACE,{"disambiguationData":[OSD([sQuery(id+"F26.wireOp",EDGE,"E121"),sQuery(id+"F26.wireOp",EDGE,"E122"),sQuery(id+"F26.wireOp",EDGE,"E123"),sQuery(id+"F26.wireOp",EDGE,"E124")])],"isStart":true}),makeQuery(id+"F27.opExtrude","CAP_FACE",FACE,{"disambiguationData":[OSD([sQuery(id+"F26.wireOp",EDGE,"E125"),sQuery(id+"F26.wireOp",EDGE,"E126"),sQuery(id+"F26.wireOp",EDGE,"E127"),sQuery(id+"F26.wireOp",EDGE,"E128")])],"isStart":true}),makeQuery(id+"F27.opExtrude","CAP_FACE",FACE,{"disambiguationData":[OSD([sQuery(id+"F26.wireOp",EDGE,"E129"),sQuery(id+"F26.wireOp",EDGE,"E130"),sQuery(id+"F26.wireOp",EDGE,"E131"),sQuery(id+"F26.wireOp",EDGE,"E132")])],"isStart":true}),makeQuery(id+"F27.opExtrude","CAP_FACE",FACE,{"disambiguationData":[OSD([sQuery(id+"F26.wireOp",EDGE,"E133"),sQuery(id+"F26.wireOp",EDGE,"E134"),sQuery(id+"F26.wireOp",EDGE,"E135"),sQuery(id+"F26.wireOp",EDGE,"E136")])],"isStart":true}),makeQuery(id+"F27.opExtrude","CAP_FACE",FACE,{"disambiguationData":[OSD([sQuery(id+"F26.wireOp",EDGE,"E137"),sQuery(id+"F26.wireOp",EDGE,"E138"),sQuery(id+"F26.wireOp",EDGE,"E139"),sQuery(id+"F26.wireOp",EDGE,"E140")])],"isStart":true})]});}
            var sketch = newSketch(context, id + "F30", { "sketchPlane" : qUnion([Q0])});
            skText(sketch, "E142", { "text": "6", "fontName": "OpenSans-Bold.ttf"});
            const initialGuessF30  = {"E142": [-0.0089, -0.01235, 1, 0, 0.02336]};
            skSetInitialGuess(sketch, initialGuessF30);
            skSolve(sketch);
        }
        {
            var Q0;
            Q0 = qSketchRegion(id + "F30", true);
            extrude(context, id + "F31", {"entities" : qUnion([Q0]), "operationType" : NewBodyOperationType.ADD, "depth" : 11.68 * mm, "offsetDistance" : 25.4 * mm});
        }
    });
